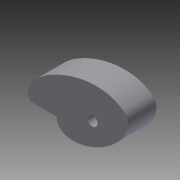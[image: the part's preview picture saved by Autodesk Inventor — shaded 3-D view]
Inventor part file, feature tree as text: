
AUTODESK INVENTOR PART (.ipt)
format: ipt  version: 2014 (Build 180170000, 170)  size: 96,768 bytes
history: native  units: in
note: dims shown in document units (in); Inventor stores cm internally (conversion verified against a paired STEP export)
features: extrude x1, sketch x1
ambient origin geometry x8: Origin, YZ Plane, XZ Plane, XY Plane, X Axis, Y Axis, Z Axis, Center Point
bodies: Solid1 (feature_tree)
feature tree (2):
  extrude  "Extrusion1"  Depth=1.4852in
  sketch  "Sketch1"  dims[d0=2.241in d2=1.4852in d3=2.6061in d4=0.5677in d5=0.4319in d6=1.3501in d7=1.396in d9=0.7824in d10=1.7203in d13=0.727in d14=0.375in d15=1.0in d16=0.0in]
